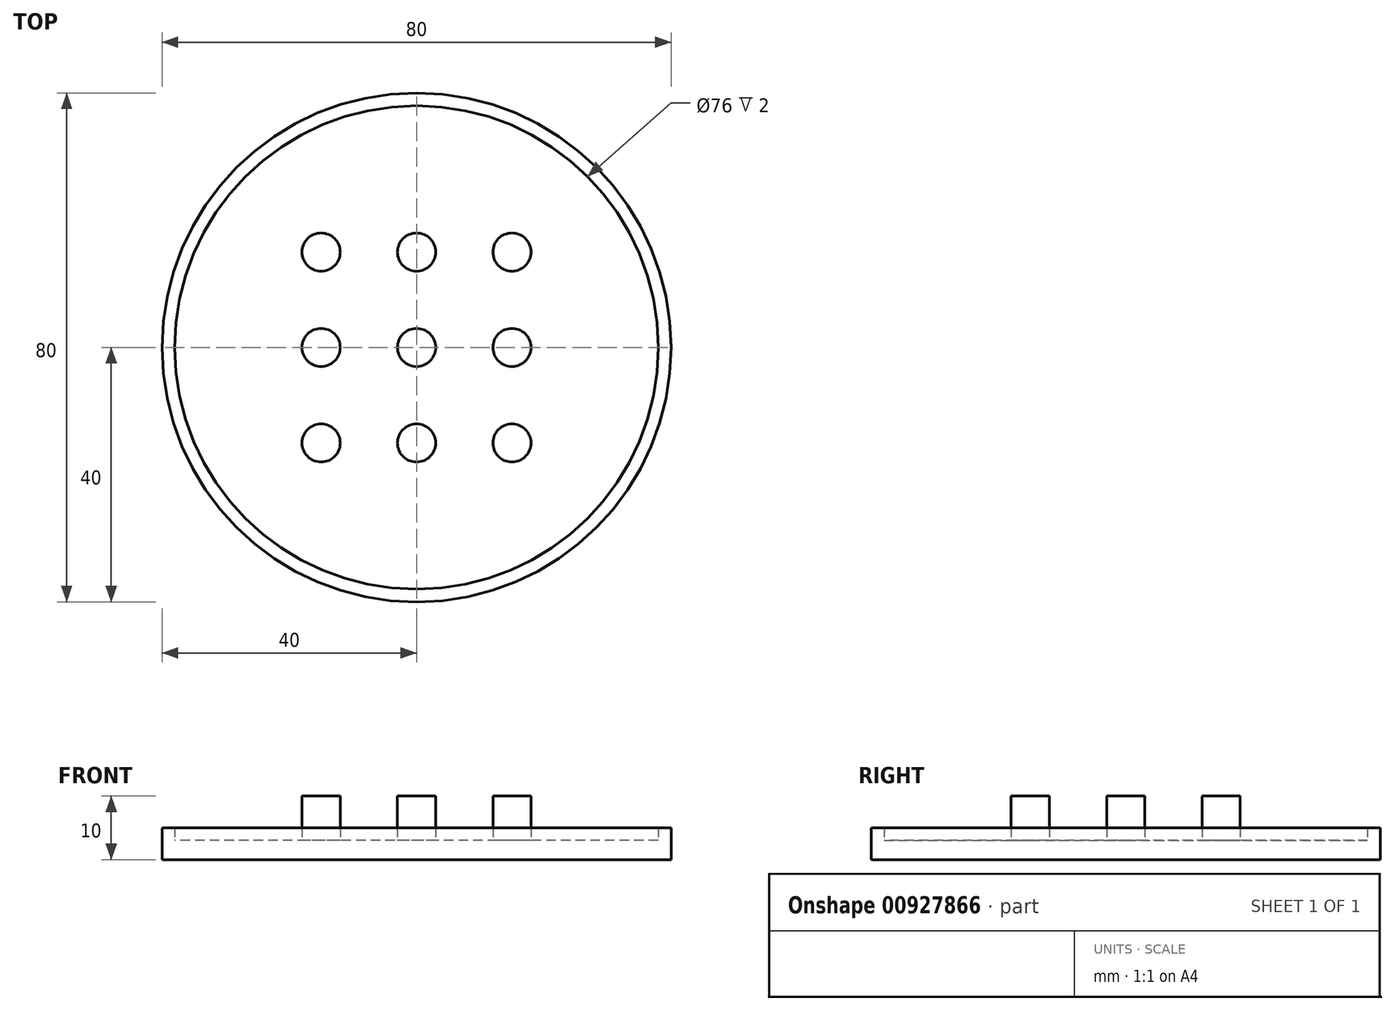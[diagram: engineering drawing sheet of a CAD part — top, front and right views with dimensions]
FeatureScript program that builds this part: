
annotation { "Feature Type Name" : "Feature", "Feature Type Description" : "" }
export const myFeature = defineFeature(function(context is Context, id is Id, definition is map)
    precondition{}
    {
        {
            var Q0;
            Q0=qCreatedBy(makeId("Top.planeOp"),FACE);
            var sketch = newSketch(context, id + "F0", { "sketchPlane" : qUnion([Q0])});
            skLineSegment(sketch, "E0", {"start": v(0, 0) * mm, "end": v(0, 15) * mm, "construction": true});
            skLineSegment(sketch, "E1", {"start": v(0, 0) * mm, "end": v(-15, 0) * mm, "construction": true});
            skCircle(sketch, "E2", {"center": v(0, 0) * mm, "radius": 40 * mm});
            skLineSegment(sketch, "E3", {"start": v(0, 0) * mm, "end": v(15, 0) * mm, "construction": true});
            skLineSegment(sketch, "E4", {"start": v(0, 0) * mm, "end": v(0, -15) * mm, "construction": true});
            skCircle(sketch, "E5", {"center": v(0, 15) * mm, "radius": 3 * mm});
            skCircle(sketch, "E6", {"center": v(-15, 0) * mm, "radius": 3 * mm});
            skCircle(sketch, "E7", {"center": v(0, -15) * mm, "radius": 3 * mm});
            skCircle(sketch, "E8", {"center": v(15, 0) * mm, "radius": 3 * mm});
            skCircle(sketch, "E9", {"center": v(0, 0) * mm, "radius": 3 * mm});
            skLineSegment(sketch, "E10.bottom", {"start": v(-15, 15) * mm, "end": v(15, 15) * mm, "construction": true});
            skLineSegment(sketch, "E10.top", {"start": v(-15, -15) * mm, "end": v(15, -15) * mm, "construction": true});
            skLineSegment(sketch, "E10.left", {"start": v(-15, 15) * mm, "end": v(-15, -15) * mm, "construction": true});
            skLineSegment(sketch, "E10.right", {"start": v(15, 15) * mm, "end": v(15, -15) * mm, "construction": true});
            skCircle(sketch, "E11", {"center": v(15, 15) * mm, "radius": 3 * mm});
            skCircle(sketch, "E12", {"center": v(-15, 15) * mm, "radius": 3 * mm});
            skCircle(sketch, "E13", {"center": v(15, -15) * mm, "radius": 3 * mm});
            skCircle(sketch, "E14", {"center": v(-15, -15) * mm, "radius": 3 * mm});
            skCircle(sketch, "E15", {"center": v(0, 0) * mm, "radius": 38 * mm});
            skSolve(sketch);
        }
        {
            var Q0;
            Q0=makeQuery(id+"F0.imprint","IMPRINT",FACE,{"disambiguationData":[TD([[makeQuery(id+"F0.imprint","IMPRINT",EDGE,{"derivedFrom":sQuery(id+"F0.wireOp",EDGE,"E5")}),-1.0]])]});
            extrude(context, id + "F1", {"entities" : qUnion([Q0]), "depth" : 3 * mm, "offsetDistance" : 25 * mm});
        }
        {
            var Q0;
            Q0=makeQuery(id+"F0.imprint","IMPRINT",FACE,{"disambiguationData":[TD([[makeQuery(id+"F0.imprint","IMPRINT",EDGE,{"derivedFrom":sQuery(id+"F0.wireOp",EDGE,"E5")}),1.0]])]});
            var Q1;
            Q1=makeQuery(id+"F0.imprint","IMPRINT",FACE,{"disambiguationData":[TD([[makeQuery(id+"F0.imprint","IMPRINT",EDGE,{"derivedFrom":sQuery(id+"F0.wireOp",EDGE,"E6")}),1.0]])]});
            var Q2;
            Q2=makeQuery(id+"F0.imprint","IMPRINT",FACE,{"disambiguationData":[TD([[makeQuery(id+"F0.imprint","IMPRINT",EDGE,{"derivedFrom":sQuery(id+"F0.wireOp",EDGE,"E7")}),1.0]])]});
            var Q3;
            Q3=makeQuery(id+"F0.imprint","IMPRINT",FACE,{"disambiguationData":[TD([[makeQuery(id+"F0.imprint","IMPRINT",EDGE,{"derivedFrom":sQuery(id+"F0.wireOp",EDGE,"E8")}),1.0]])]});
            var Q4;
            Q4=makeQuery(id+"F0.imprint","IMPRINT",FACE,{"disambiguationData":[TD([[makeQuery(id+"F0.imprint","IMPRINT",EDGE,{"derivedFrom":sQuery(id+"F0.wireOp",EDGE,"E12")}),1.0]])]});
            var Q5;
            Q5=makeQuery(id+"F0.imprint","IMPRINT",FACE,{"disambiguationData":[TD([[makeQuery(id+"F0.imprint","IMPRINT",EDGE,{"derivedFrom":sQuery(id+"F0.wireOp",EDGE,"E11")}),1.0]])]});
            var Q6;
            Q6=makeQuery(id+"F0.imprint","IMPRINT",FACE,{"disambiguationData":[TD([[makeQuery(id+"F0.imprint","IMPRINT",EDGE,{"derivedFrom":sQuery(id+"F0.wireOp",EDGE,"E13")}),1.0]])]});
            var Q7;
            Q7=makeQuery(id+"F0.imprint","IMPRINT",FACE,{"disambiguationData":[TD([[makeQuery(id+"F0.imprint","IMPRINT",EDGE,{"derivedFrom":sQuery(id+"F0.wireOp",EDGE,"E9")}),1.0]])]});
            var Q8;
            Q8=makeQuery(id+"F0.imprint","IMPRINT",FACE,{"disambiguationData":[TD([[makeQuery(id+"F0.imprint","IMPRINT",EDGE,{"derivedFrom":sQuery(id+"F0.wireOp",EDGE,"E14")}),1.0]])]});
            extrude(context, id + "F2", {"entities" : qUnion([Q0, Q1, Q2, Q3, Q4, Q5, Q6, Q7, Q8]), "operationType" : NewBodyOperationType.ADD, "depth" : 10 * mm, "offsetDistance" : 25 * mm});
        }
        {
            var Q0;
            Q0=makeQuery(id+"F0.imprint","IMPRINT",FACE,{"disambiguationData":[TD([[makeQuery(id+"F0.imprint","IMPRINT",EDGE,{"derivedFrom":sQuery(id+"F0.wireOp",EDGE,"E2")}),1.0]])]});
            extrude(context, id + "F3", {"entities" : qUnion([Q0]), "operationType" : NewBodyOperationType.ADD, "depth" : 5 * mm, "offsetDistance" : 25 * mm});
        }
    });
